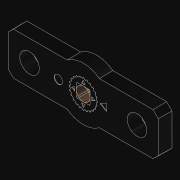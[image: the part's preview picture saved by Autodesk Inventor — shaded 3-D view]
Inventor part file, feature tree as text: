
AUTODESK INVENTOR PART (.ipt)
format: ipt  version: 2021.3 (Build 253353010, 353A)  size: 954,368 bytes
history: native  units: in
note: dims shown in document units (in); Inventor stores cm internally (conversion verified against a paired STEP export)
features: other x3, imported_body x2, sketch x1, extrude x1
ambient origin geometry x8: Origin, YZ Plane, XZ Plane, XY Plane, X Axis, Y Axis, Z Axis, Center Point
bodies: Body1 (feature_tree), Body2 (feature_tree), Body3 (feature_tree)
feature tree (7):
  parser-record x1  (decoder bookkeeping rows leaked as tree rows — omitted from the tree; the rows remain in map.json)
  imported_body  "Base1"
  imported_body  "Base2"
  other  "NONE_1"
  sketch  "Sketch1"  dims[d0=0.3937in d1=0.0in]
  other  "Srf1"
  extrude  "ExtrusionSrf1"  [1 undecoded]
note: 1 required parameter value undecoded (feature->parameter linkage not recoverable at this tier; creation-order binding heuristic only, values carry confidence <= 0.55)
